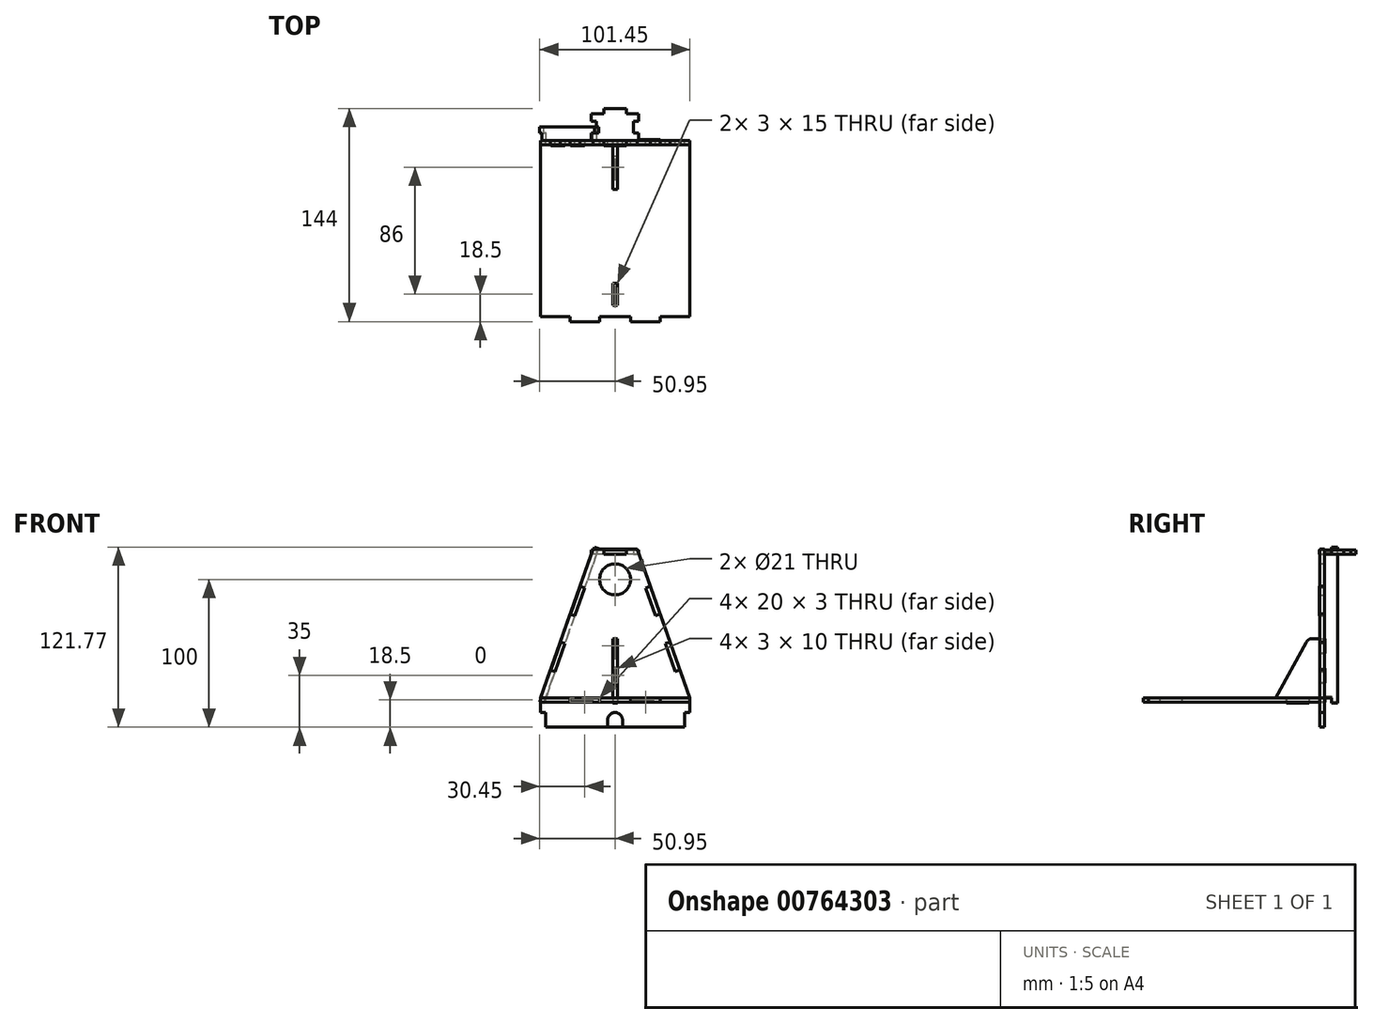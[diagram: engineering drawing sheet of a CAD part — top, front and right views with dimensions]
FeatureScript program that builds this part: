
annotation { "Feature Type Name" : "Feature", "Feature Type Description" : "" }
export const myFeature = defineFeature(function(context is Context, id is Id, definition is map)
    precondition{}
    {
        {
            var Q0;
            Q0=qCreatedBy(makeId("Front.planeOp"),FACE);
            var sketch = newSketch(context, id + "F0", { "sketchPlane" : qUnion([Q0])});
            skCircle(sketch, "E0", {"center": v(0, 0) * mm, "radius": 10.5 * mm});
            skLineSegment(sketch, "E1", {"start": v(15, 20.5) * mm, "end": v(23.85, -4.57) * mm});
            skLineSegment(sketch, "E2", {"start": v(50.5, -80) * mm, "end": v(50.5, -90) * mm});
            skLineSegment(sketch, "E3", {"start": v(50.5, -90) * mm, "end": v(47, -90) * mm});
            skLineSegment(sketch, "E4", {"start": v(47, -90) * mm, "end": v(47, -100) * mm});
            skLineSegment(sketch, "E5", {"start": v(47, -100) * mm, "end": v(-47, -100) * mm});
            skLineSegment(sketch, "E6", {"start": v(-47, -100) * mm, "end": v(-47, -90) * mm});
            skLineSegment(sketch, "E7", {"start": v(-47, -90) * mm, "end": v(-50.5, -90) * mm});
            skLineSegment(sketch, "E8", {"start": v(-50.5, -90) * mm, "end": v(-50.5, -80) * mm});
            skLineSegment(sketch, "E9", {"start": v(-50.5, -80) * mm, "end": v(-43.84, -61.14) * mm});
            skLineSegment(sketch, "E10.bottom", {"start": v(-30.5, -80) * mm, "end": v(-10.5, -80) * mm});
            skLineSegment(sketch, "E10.top", {"start": v(-30.5, -83) * mm, "end": v(-10.5, -83) * mm});
            skLineSegment(sketch, "E10.left", {"start": v(-30.5, -80) * mm, "end": v(-30.5, -83) * mm});
            skLineSegment(sketch, "E10.right", {"start": v(-10.5, -80) * mm, "end": v(-10.5, -83) * mm});
            skLineSegment(sketch, "E11.bottom", {"start": v(10.5, -80) * mm, "end": v(30.5, -80) * mm});
            skLineSegment(sketch, "E11.top", {"start": v(10.5, -83) * mm, "end": v(30.5, -83) * mm});
            skLineSegment(sketch, "E11.left", {"start": v(10.5, -80) * mm, "end": v(10.5, -83) * mm});
            skLineSegment(sketch, "E11.right", {"start": v(30.5, -80) * mm, "end": v(30.5, -83) * mm});
            skLineSegment(sketch, "E12", {"start": v(-10.5, -80) * mm, "end": v(0, 0) * mm, "construction": true});
            skLineSegment(sketch, "E13", {"start": v(10.5, -80) * mm, "end": v(0, 0) * mm, "construction": true});
            skLineSegment(sketch, "E14", {"start": v(15, 20.5) * mm, "end": v(7.5, 20.5) * mm});
            skLineSegment(sketch, "E15", {"start": v(15, 20.5) * mm, "end": v(0, 0) * mm, "construction": true});
            skLineSegment(sketch, "E16", {"start": v(-15, 20.5) * mm, "end": v(0, 0) * mm, "construction": true});
            skLineSegment(sketch, "E17", {"start": v(5, -100) * mm, "end": v(5, -95) * mm});
            skArc(sketch, "E18", {"start": v(5, -95) * mm, "mid": v(0, -90) * mm, "end": v(-5, -95) * mm});
            skLineSegment(sketch, "E19", {"start": v(-5, -95) * mm, "end": v(-5, -100) * mm});
            skLineSegment(sketch, "E20", {"start": v(0, -95) * mm, "end": v(0, -100) * mm, "construction": true});
            skLineSegment(sketch, "E21", {"start": v(7.5, 20.5) * mm, "end": v(7.5, 17) * mm});
            skLineSegment(sketch, "E22", {"start": v(7.5, 17) * mm, "end": v(-7.5, 17) * mm});
            skLineSegment(sketch, "E23", {"start": v(-7.5, 17) * mm, "end": v(-7.5, 20.5) * mm});
            skLineSegment(sketch, "E24.trimOffspring", {"start": v(-7.5, 20.5) * mm, "end": v(-15, 20.5) * mm});
            skLineSegment(sketch, "E25", {"start": v(23.85, -4.57) * mm, "end": v(20.55, -5.73) * mm});
            skLineSegment(sketch, "E26", {"start": v(20.55, -5.73) * mm, "end": v(27.22, -24.6) * mm});
            skLineSegment(sketch, "E27", {"start": v(27.22, -24.6) * mm, "end": v(30.52, -23.43) * mm});
            skLineSegment(sketch, "E28", {"start": v(37.18, -42.28) * mm, "end": v(33.88, -43.45) * mm});
            skLineSegment(sketch, "E29", {"start": v(33.88, -43.45) * mm, "end": v(40.54, -62.3) * mm});
            skLineSegment(sketch, "E30", {"start": v(40.54, -62.3) * mm, "end": v(43.84, -61.14) * mm});
            skLineSegment(sketch, "E31.trimOffspring", {"start": v(30.52, -23.43) * mm, "end": v(37.18, -42.28) * mm});
            skLineSegment(sketch, "E32.trimOffspring", {"start": v(43.84, -61.14) * mm, "end": v(50.5, -80) * mm});
            skLineSegment(sketch, "E33", {"start": v(10.5, -83) * mm, "end": v(0, -95) * mm, "construction": true});
            skLineSegment(sketch, "E34", {"start": v(0, -95) * mm, "end": v(-10.5, -83) * mm, "construction": true});
            skLineSegment(sketch, "E35", {"start": v(-23.85, -4.57) * mm, "end": v(-20.55, -5.73) * mm});
            skLineSegment(sketch, "E36", {"start": v(-20.55, -5.73) * mm, "end": v(-27.22, -24.6) * mm});
            skLineSegment(sketch, "E37", {"start": v(-27.22, -24.6) * mm, "end": v(-30.52, -23.43) * mm});
            skLineSegment(sketch, "E38", {"start": v(-37.18, -42.28) * mm, "end": v(-33.88, -43.45) * mm});
            skLineSegment(sketch, "E39", {"start": v(-33.88, -43.45) * mm, "end": v(-40.54, -62.3) * mm});
            skLineSegment(sketch, "E40", {"start": v(-40.54, -62.3) * mm, "end": v(-43.84, -61.14) * mm});
            skLineSegment(sketch, "E41.trimOffspring", {"start": v(-23.85, -4.57) * mm, "end": v(-15, 20.5) * mm});
            skLineSegment(sketch, "E42.trimOffspring", {"start": v(-37.18, -42.28) * mm, "end": v(-30.52, -23.43) * mm});
            skLineSegment(sketch, "E43", {"start": v(-43.84, -61.14) * mm, "end": v(-37.18, -42.28) * mm});
            skLineSegment(sketch, "E44", {"start": v(-30.52, -23.43) * mm, "end": v(-23.85, -4.57) * mm});
            skLineSegment(sketch, "E45", {"start": v(23.85, -4.57) * mm, "end": v(30.52, -23.43) * mm});
            skLineSegment(sketch, "E46", {"start": v(37.18, -42.28) * mm, "end": v(43.84, -61.14) * mm});
            skLineSegment(sketch, "E47", {"start": v(-7.5, 20.5) * mm, "end": v(7.5, 20.5) * mm});
            skLineSegment(sketch, "E48.bottom", {"start": v(-1.5, -40) * mm, "end": v(1.5, -40) * mm});
            skLineSegment(sketch, "E48.top", {"start": v(-1.5, -50) * mm, "end": v(1.5, -50) * mm});
            skLineSegment(sketch, "E48.left", {"start": v(-1.5, -40) * mm, "end": v(-1.5, -50) * mm});
            skLineSegment(sketch, "E48.right", {"start": v(1.5, -40) * mm, "end": v(1.5, -50) * mm});
            skLineSegment(sketch, "E49.bottom", {"start": v(-1.5, -60) * mm, "end": v(1.5, -60) * mm});
            skLineSegment(sketch, "E49.top", {"start": v(-1.5, -70) * mm, "end": v(1.5, -70) * mm});
            skLineSegment(sketch, "E49.left", {"start": v(-1.5, -60) * mm, "end": v(-1.5, -70) * mm});
            skLineSegment(sketch, "E49.right", {"start": v(1.5, -60) * mm, "end": v(1.5, -70) * mm});
            skLineSegment(sketch, "E50", {"start": v(-10.5, -80) * mm, "end": v(10.5, -80) * mm, "construction": true});
            skLineSegment(sketch, "E51", {"start": v(0, -80) * mm, "end": v(0, -70) * mm, "construction": true});
            skLineSegment(sketch, "E52", {"start": v(0, -60) * mm, "end": v(0, -50) * mm, "construction": true});
            skSolve(sketch);
        }
        {
            var Q0;
            Q0=makeQuery(id+"F0.imprint","IMPRINT",FACE,{"disambiguationData":[TD([[makeQuery(id+"F0.imprint","IMPRINT",EDGE,{"derivedFrom":sQuery(id+"F0.wireOp",EDGE,"E0")}),-1.0]])]});
            extrude(context, id + "F1", {"entities" : qUnion([Q0]), "depth" : 3 * mm, "offsetDistance" : 25 * mm});
        }
        {
            var Q0;
            Q0 = qSketchRegion(id + "F0", true);
            extrude(context, id + "F2", {"entities" : qUnion([Q0]), "depth" : 3 * mm, "offsetDistance" : 25 * mm});
        }
        {
            var Q0;
            Q0=makeQuery(id+"F1.opExtrude","SWEPT_FACE",FACE,{"disambiguationData":[OSD([sQuery(id+"F0.wireOp",EDGE,"E36")])]});
            var sketch = newSketch(context, id + "F3", { "sketchPlane" : qUnion([Q0])});
            skLineSegment(sketch, "E53", {"start": v(-5, 11.86) * mm, "end": v(0, 11.86) * mm});
            skLineSegment(sketch, "E54", {"start": v(0, 11.86) * mm, "end": v(0, -12.25) * mm});
            skLineSegment(sketch, "E55", {"start": v(0, -12.25) * mm, "end": v(3.5, -12.25) * mm});
            skLineSegment(sketch, "E56", {"start": v(3.5, -12.25) * mm, "end": v(3.5, -32.25) * mm});
            skLineSegment(sketch, "E57", {"start": v(3.5, -32.25) * mm, "end": v(0, -32.25) * mm});
            skLineSegment(sketch, "E58", {"start": v(0, -32.25) * mm, "end": v(0, -52.25) * mm});
            skLineSegment(sketch, "E59", {"start": v(0, -52.25) * mm, "end": v(3.5, -52.25) * mm});
            skLineSegment(sketch, "E60", {"start": v(3.5, -52.25) * mm, "end": v(3.5, -72.25) * mm});
            skLineSegment(sketch, "E61", {"start": v(3.5, -72.25) * mm, "end": v(0, -72.25) * mm});
            skLineSegment(sketch, "E62", {"start": v(0, -72.25) * mm, "end": v(0, -91.02) * mm});
            skLineSegment(sketch, "E63", {"start": v(0, -91.02) * mm, "end": v(-5, -91.02) * mm});
            skLineSegment(sketch, "E64", {"start": v(-5, -91.02) * mm, "end": v(-5, -95.02) * mm});
            skLineSegment(sketch, "E65", {"start": v(-5, -95.02) * mm, "end": v(-9, -95.02) * mm});
            skLineSegment(sketch, "E66", {"start": v(-9, -95.02) * mm, "end": v(-9, 15.86) * mm});
            skLineSegment(sketch, "E67", {"start": v(-9, 15.86) * mm, "end": v(-5, 15.86) * mm});
            skLineSegment(sketch, "E68", {"start": v(-5, 15.86) * mm, "end": v(-5, 11.86) * mm});
            skSolve(sketch);
        }
        {
            var Q0;
            Q0 = qSketchRegion(id + "F3", true);
            extrude(context, id + "F4", {"entities" : qUnion([Q0]), "depth" : 3 * mm, "offsetDistance" : 25 * mm});
        }
        {
            var Q0;
            Q0=makeQuery(id+"F1.opExtrude","SWEPT_FACE",FACE,{"disambiguationData":[OSD([sQuery(id+"F0.wireOp",EDGE,"E22")])]});
            var sketch = newSketch(context, id + "F5", { "sketchPlane" : qUnion([Q0])});
            skLineSegment(sketch, "E69", {"start": v(-7.5, 0) * mm, "end": v(-16.02, 0) * mm});
            skLineSegment(sketch, "E70", {"start": v(-16.02, 0) * mm, "end": v(-16.02, 5) * mm});
            skLineSegment(sketch, "E71", {"start": v(-16.02, 5) * mm, "end": v(-12.52, 5) * mm});
            skLineSegment(sketch, "E72", {"start": v(-12.52, 5) * mm, "end": v(-12.52, 13) * mm});
            skLineSegment(sketch, "E73", {"start": v(-12.52, 13) * mm, "end": v(-16.02, 13) * mm});
            skLineSegment(sketch, "E74", {"start": v(-16.02, 13) * mm, "end": v(-16.02, 18) * mm});
            skLineSegment(sketch, "E75", {"start": v(-16.02, 18) * mm, "end": v(-7.5, 18) * mm});
            skLineSegment(sketch, "E76", {"start": v(-7.5, 18) * mm, "end": v(-7.5, 21.5) * mm});
            skLineSegment(sketch, "E77", {"start": v(-7.5, 21.5) * mm, "end": v(7.5, 21.5) * mm});
            skLineSegment(sketch, "E78", {"start": v(7.5, 21.5) * mm, "end": v(7.5, 18) * mm});
            skLineSegment(sketch, "E79", {"start": v(7.5, 18) * mm, "end": v(16.02, 18) * mm});
            skLineSegment(sketch, "E80", {"start": v(16.02, 18) * mm, "end": v(16.02, 13) * mm});
            skLineSegment(sketch, "E81", {"start": v(16.02, 13) * mm, "end": v(12.52, 13) * mm});
            skLineSegment(sketch, "E82", {"start": v(12.52, 13) * mm, "end": v(12.52, 5) * mm});
            skLineSegment(sketch, "E83", {"start": v(12.52, 5) * mm, "end": v(16.02, 5) * mm});
            skLineSegment(sketch, "E84", {"start": v(16.02, 5) * mm, "end": v(16.02, 0) * mm});
            skLineSegment(sketch, "E85", {"start": v(16.02, 0) * mm, "end": v(7.5, 0) * mm});
            skLineSegment(sketch, "E86", {"start": v(7.5, 0) * mm, "end": v(7.5, -3.5) * mm});
            skLineSegment(sketch, "E87", {"start": v(7.5, -3.5) * mm, "end": v(-7.5, -3.5) * mm});
            skLineSegment(sketch, "E88", {"start": v(-7.5, -3.5) * mm, "end": v(-7.5, 0) * mm});
            skSolve(sketch);
        }
        {
            var Q0;
            Q0 = qSketchRegion(id + "F5", true);
            extrude(context, id + "F6", {"entities" : qUnion([Q0]), "depth" : 3 * mm, "offsetDistance" : 25 * mm});
        }
        {
            var Q0;
            Q0=makeQuery(id+"F1.opExtrude","SWEPT_FACE",FACE,{"disambiguationData":[OSD([sQuery(id+"F0.wireOp",EDGE,"E48.right")])]});
            var sketch = newSketch(context, id + "F7", { "sketchPlane" : qUnion([Q0])});
            skLineSegment(sketch, "E89", {"start": v(8, -40) * mm, "end": v(-0.5, -40) * mm});
            skLineSegment(sketch, "E90", {"start": v(-0.5, -40) * mm, "end": v(-0.5, -50) * mm});
            skLineSegment(sketch, "E91", {"start": v(-0.5, -50) * mm, "end": v(3, -50) * mm});
            skLineSegment(sketch, "E92", {"start": v(3, -50) * mm, "end": v(3, -60) * mm});
            skLineSegment(sketch, "E93", {"start": v(3, -60) * mm, "end": v(-0.5, -60) * mm});
            skLineSegment(sketch, "E94", {"start": v(-0.5, -60) * mm, "end": v(-0.5, -70) * mm});
            skLineSegment(sketch, "E95", {"start": v(-0.5, -70) * mm, "end": v(3, -70) * mm});
            skLineSegment(sketch, "E96", {"start": v(3, -70) * mm, "end": v(3, -80) * mm});
            skLineSegment(sketch, "E97", {"start": v(3, -80) * mm, "end": v(10.5, -80) * mm});
            skLineSegment(sketch, "E98", {"start": v(10.5, -80) * mm, "end": v(10.5, -83.5) * mm});
            skLineSegment(sketch, "E99", {"start": v(10.5, -83.5) * mm, "end": v(25.5, -83.5) * mm});
            skLineSegment(sketch, "E100", {"start": v(25.5, -83.5) * mm, "end": v(25.5, -80) * mm});
            skLineSegment(sketch, "E101", {"start": v(25.5, -80) * mm, "end": v(33, -80) * mm});
            skLineSegment(sketch, "E102", {"start": v(33, -80) * mm, "end": v(12.38, -42.59) * mm});
            skArc(sketch, "E103", {"start": v(12.38, -42.59) * mm, "mid": v(10.54, -40.7) * mm, "end": v(8, -40) * mm});
            skSolve(sketch);
        }
        {
            var Q0;
            Q0 = qSketchRegion(id + "F7", true);
            extrude(context, id + "F8", {"entities" : qUnion([Q0]), "depth" : 3 * mm, "offsetDistance" : 25 * mm});
        }
        {
            var Q0;
            Q0=makeQuery(id+"F1.opExtrude","SWEPT_FACE",FACE,{"disambiguationData":[OSD([sQuery(id+"F0.wireOp",EDGE,"E10.top")])]});
            var sketch = newSketch(context, id + "F9", { "sketchPlane" : qUnion([Q0])});
            skLineSegment(sketch, "E104", {"start": v(-50.5, -3) * mm, "end": v(-30.5, -3) * mm});
            skLineSegment(sketch, "E105", {"start": v(-30.5, -3) * mm, "end": v(-30.5, 0.5) * mm});
            skLineSegment(sketch, "E106", {"start": v(-30.5, 0.5) * mm, "end": v(-10.5, 0.5) * mm});
            skLineSegment(sketch, "E107", {"start": v(-10.5, 0.5) * mm, "end": v(-10.5, -3) * mm});
            skLineSegment(sketch, "E108", {"start": v(-10.5, -3) * mm, "end": v(10.5, -3) * mm});
            skLineSegment(sketch, "E109", {"start": v(10.5, -3) * mm, "end": v(10.5, 0.5) * mm});
            skLineSegment(sketch, "E110", {"start": v(10.5, 0.5) * mm, "end": v(30.5, 0.5) * mm});
            skLineSegment(sketch, "E111", {"start": v(30.5, 0.5) * mm, "end": v(30.5, -3) * mm});
            skLineSegment(sketch, "E112", {"start": v(30.5, -3) * mm, "end": v(50.5, -3) * mm});
            skLineSegment(sketch, "E113", {"start": v(50.5, -3) * mm, "end": v(50.5, -119) * mm});
            skLineSegment(sketch, "E114", {"start": v(50.5, -119) * mm, "end": v(30.5, -119) * mm});
            skLineSegment(sketch, "E115", {"start": v(30.5, -119) * mm, "end": v(30.5, -122.5) * mm});
            skLineSegment(sketch, "E116", {"start": v(30.5, -122.5) * mm, "end": v(10.5, -122.5) * mm});
            skLineSegment(sketch, "E117", {"start": v(10.5, -122.5) * mm, "end": v(10.5, -119) * mm});
            skLineSegment(sketch, "E118", {"start": v(10.5, -119) * mm, "end": v(-10.5, -119) * mm});
            skLineSegment(sketch, "E119", {"start": v(-10.5, -119) * mm, "end": v(-10.5, -122.5) * mm});
            skLineSegment(sketch, "E120", {"start": v(-10.5, -122.5) * mm, "end": v(-30.5, -122.5) * mm});
            skLineSegment(sketch, "E121", {"start": v(-30.5, -122.5) * mm, "end": v(-30.5, -119) * mm});
            skLineSegment(sketch, "E122", {"start": v(-30.5, -119) * mm, "end": v(-50.5, -119) * mm});
            skLineSegment(sketch, "E123", {"start": v(-50.5, -119) * mm, "end": v(-50.5, -3) * mm});
            skLineSegment(sketch, "E124.bottom", {"start": v(-1.5, -25.5) * mm, "end": v(1.5, -25.5) * mm});
            skLineSegment(sketch, "E124.top", {"start": v(-1.5, -10.5) * mm, "end": v(1.5, -10.5) * mm});
            skLineSegment(sketch, "E124.left", {"start": v(-1.5, -25.5) * mm, "end": v(-1.5, -10.5) * mm});
            skLineSegment(sketch, "E124.right", {"start": v(1.5, -25.5) * mm, "end": v(1.5, -10.5) * mm});
            skLineSegment(sketch, "E125", {"start": v(-50.5, -61) * mm, "end": v(50.5, -61) * mm, "construction": true});
            skLineSegment(sketch, "E126.MirrorCS", {"start": v(-1.5, -96.5) * mm, "end": v(1.5, -96.5) * mm});
            skLineSegment(sketch, "E127.MirrorCS", {"start": v(-1.5, -111.5) * mm, "end": v(1.5, -111.5) * mm});
            skLineSegment(sketch, "E128.MirrorCS", {"start": v(1.5, -96.5) * mm, "end": v(1.5, -111.5) * mm});
            skLineSegment(sketch, "E129.MirrorCS", {"start": v(-1.5, -96.5) * mm, "end": v(-1.5, -111.5) * mm});
            skSolve(sketch);
        }
        {
            var Q0;
            Q0 = qSketchRegion(id + "F9", true);
            extrude(context, id + "F10", {"entities" : qUnion([Q0]), "depth" : 3 * mm, "offsetDistance" : 25 * mm});
        }
    });
